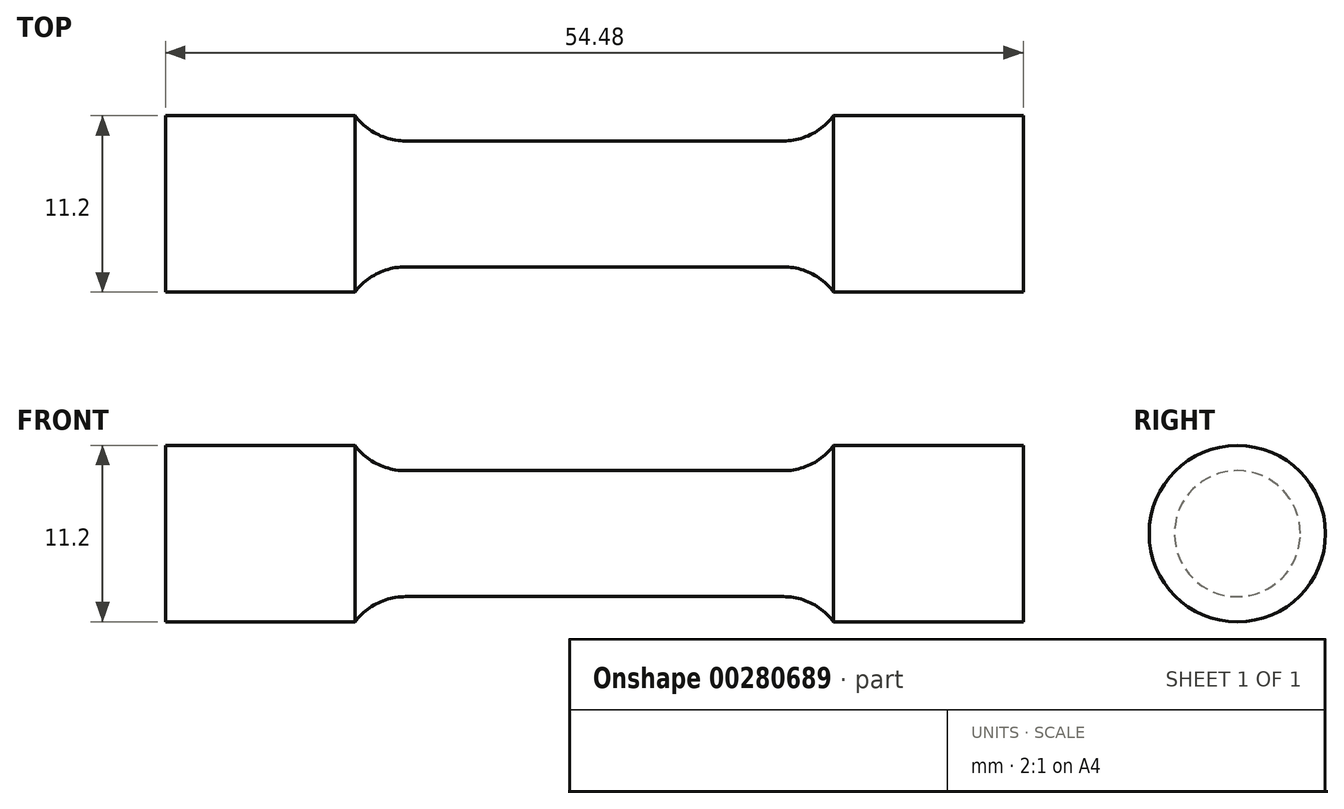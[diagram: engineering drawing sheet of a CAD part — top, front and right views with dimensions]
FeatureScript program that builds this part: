
annotation { "Feature Type Name" : "Feature", "Feature Type Description" : "" }
export const myFeature = defineFeature(function(context is Context, id is Id, definition is map)
    precondition{}
    {
        {
            var Q0;
            Q0=qCreatedBy(makeId("Front.planeOp"),FACE);
            var sketch = newSketch(context, id + "F0", { "sketchPlane" : qUnion([Q0])});
            skLineSegment(sketch, "E0", {"start": v(0, 4) * mm, "end": v(12, 4) * mm});
            skArc(sketch, "E1", {"start": v(12, 4) * mm, "mid": v(13.79, 4.42) * mm, "end": v(15.2, 5.6) * mm});
            skLineSegment(sketch, "E2", {"start": v(15.2, 5.6) * mm, "end": v(27.24, 5.6) * mm});
            skLineSegment(sketch, "E3", {"start": v(27.24, 5.6) * mm, "end": v(27.24, 0) * mm});
            skLineSegment(sketch, "E4.MirrorCS", {"start": v(0, 4) * mm, "end": v(-12, 4) * mm});
            skArc(sketch, "E5.MirrorCS", {"start": v(-12, 4) * mm, "mid": v(-13.79, 4.42) * mm, "end": v(-15.2, 5.6) * mm});
            skLineSegment(sketch, "E6.MirrorCS", {"start": v(-15.2, 5.6) * mm, "end": v(-27.24, 5.6) * mm});
            skLineSegment(sketch, "E7.MirrorCS", {"start": v(-27.24, 5.6) * mm, "end": v(-27.24, 0) * mm});
            skLineSegment(sketch, "E8", {"start": v(-27.24, 0) * mm, "end": v(27.24, 0) * mm});
            skSolve(sketch);
        }
        {
            var Q0;
            Q0 = qSketchRegion(id + "F0", true);
            var Q1;
            Q1=sQuery(id+"F0.wireOp",EDGE,"E8");
            revolve(context, id + "F1", {"entities" : qUnion([Q0]), "axis" : qUnion([Q1]), "revolveType" : RevolveType.FULL});
        }
    });
